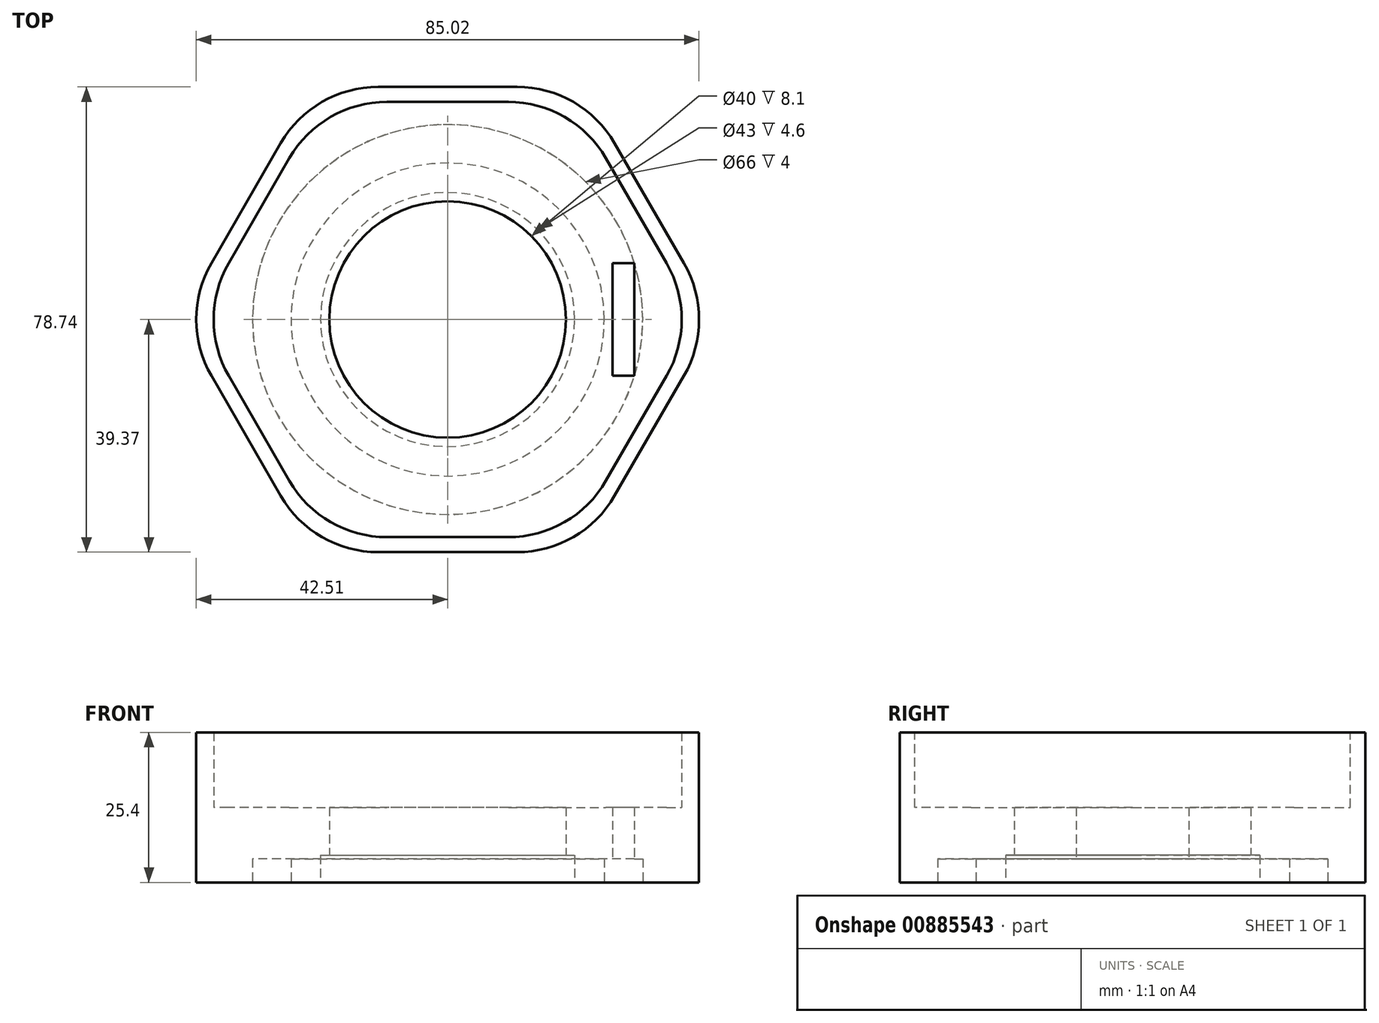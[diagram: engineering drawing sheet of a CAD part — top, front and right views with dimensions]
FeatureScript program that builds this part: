
annotation { "Feature Type Name" : "Feature", "Feature Type Description" : "" }
export const myFeature = defineFeature(function(context is Context, id is Id, definition is map)
    precondition{}
    {
        {
            var Q0;
            Q0=qCreatedBy(makeId("Top.planeOp"),FACE);
            var sketch = newSketch(context, id + "F0", { "sketchPlane" : qUnion([Q0])});
            skCircle(sketch, "E0.cCircle", {"center": v(0, 0) * mm, "radius": 39.37 * mm, "construction": true});
            skLineSegment(sketch, "E0.0", {"start": v(-22.73, 39.37) * mm, "end": v(22.73, 39.37) * mm});
            skLineSegment(sketch, "E0.1", {"start": v(22.73, 39.37) * mm, "end": v(45.46, 0) * mm});
            skLineSegment(sketch, "E0.2", {"start": v(45.46, 0) * mm, "end": v(22.73, -39.37) * mm});
            skLineSegment(sketch, "E0.3", {"start": v(22.73, -39.37) * mm, "end": v(-22.73, -39.37) * mm});
            skLineSegment(sketch, "E0.4", {"start": v(-22.73, -39.37) * mm, "end": v(-45.46, 0) * mm});
            skLineSegment(sketch, "E0.5", {"start": v(-45.46, 0) * mm, "end": v(-22.73, 39.37) * mm});
            skPoint(sketch, "E0.0.midPoint", {"position": v(0, 39.37) * mm});
            skSolve(sketch);
        }
        {
            var Q0;
            Q0=makeQuery(id+"F0.imprint","IMPRINT",FACE,{"disambiguationData":[TD([[makeQuery(id+"F0.imprint","IMPRINT",EDGE,{"derivedFrom":sQuery(id+"F0.wireOp",EDGE,"E0.0")}),-1.0]])]});
            extrude(context, id + "F1", {"entities" : qUnion([Q0]), "depth" : 25.4 * mm, "offsetDistance" : 25.4 * mm});
        }
        {
            var Q0;
            Q0=makeQuery(id+"F1.opExtrude","CAP_FACE",FACE,{"disambiguationData":[OSD([sQuery(id+"F0.wireOp",EDGE,"E0.0"),sQuery(id+"F0.wireOp",EDGE,"E0.1"),sQuery(id+"F0.wireOp",EDGE,"E0.2"),sQuery(id+"F0.wireOp",EDGE,"E0.3"),sQuery(id+"F0.wireOp",EDGE,"E0.4"),sQuery(id+"F0.wireOp",EDGE,"E0.5")])],"isStart":false});
            var sketch = newSketch(context, id + "F2", { "sketchPlane" : qUnion([Q0])});
            skCircle(sketch, "E1.cCircle", {"center": v(0, 0) * mm, "radius": 36.83 * mm, "construction": true});
            skLineSegment(sketch, "E1.0", {"start": v(-21.26, 36.83) * mm, "end": v(21.26, 36.83) * mm});
            skLineSegment(sketch, "E1.1", {"start": v(21.26, 36.83) * mm, "end": v(42.53, 0) * mm});
            skLineSegment(sketch, "E1.2", {"start": v(42.53, 0) * mm, "end": v(21.26, -36.83) * mm});
            skLineSegment(sketch, "E1.3", {"start": v(21.26, -36.83) * mm, "end": v(-21.26, -36.83) * mm});
            skLineSegment(sketch, "E1.4", {"start": v(-21.26, -36.83) * mm, "end": v(-42.53, 0) * mm});
            skLineSegment(sketch, "E1.5", {"start": v(-42.53, 0) * mm, "end": v(-21.26, 36.83) * mm});
            skPoint(sketch, "E1.0.midPoint", {"position": v(0, 36.83) * mm});
            skSolve(sketch);
        }
        {
            var Q0;
            Q0=makeQuery(id+"F2.imprint","IMPRINT",FACE,{"disambiguationData":[TD([[makeQuery(id+"F2.imprint","IMPRINT",EDGE,{"derivedFrom":sQuery(id+"F2.wireOp",EDGE,"E1.0")}),-1.0]])]});
            extrude(context, id + "F3", {"entities" : qUnion([Q0]), "operationType" : NewBodyOperationType.REMOVE, "oppositeDirection" : true, "depth" : 12.7 * mm, "offsetDistance" : 25.4 * mm});
        }
        {
            var Q0;
            Q0=makeQuery(id+"F3.boolean.opBoolean","COPY",EDGE,{"derivedFrom":makeQuery(id+"F3.opExtrude","SWEPT_EDGE",EDGE,{"disambiguationData":[OSD([sQuery(id+"F2.wireOp",EDGE,"E1.0"),sQuery(id+"F2.wireOp",EDGE,"E1.1")])]})});
            var Q1;
            Q1=makeQuery(id+"F3.boolean.opBoolean","COPY",EDGE,{"derivedFrom":makeQuery(id+"F3.opExtrude","SWEPT_EDGE",EDGE,{"disambiguationData":[OSD([sQuery(id+"F2.wireOp",EDGE,"E1.0"),sQuery(id+"F2.wireOp",EDGE,"E1.5")])]})});
            var Q2;
            Q2=makeQuery(id+"F3.boolean.opBoolean","COPY",EDGE,{"derivedFrom":makeQuery(id+"F3.opExtrude","SWEPT_EDGE",EDGE,{"disambiguationData":[OSD([sQuery(id+"F2.wireOp",EDGE,"E1.4"),sQuery(id+"F2.wireOp",EDGE,"E1.5")])]})});
            var Q3;
            Q3=makeQuery(id+"F3.boolean.opBoolean","COPY",EDGE,{"derivedFrom":makeQuery(id+"F3.opExtrude","SWEPT_EDGE",EDGE,{"disambiguationData":[OSD([sQuery(id+"F2.wireOp",EDGE,"E1.1"),sQuery(id+"F2.wireOp",EDGE,"E1.2")])]})});
            var Q4;
            Q4=makeQuery(id+"F3.boolean.opBoolean","COPY",EDGE,{"derivedFrom":makeQuery(id+"F3.opExtrude","SWEPT_EDGE",EDGE,{"disambiguationData":[OSD([sQuery(id+"F2.wireOp",EDGE,"E1.2"),sQuery(id+"F2.wireOp",EDGE,"E1.3")])]})});
            var Q5;
            Q5=makeQuery(id+"F3.boolean.opBoolean","COPY",EDGE,{"derivedFrom":makeQuery(id+"F3.opExtrude","SWEPT_EDGE",EDGE,{"disambiguationData":[OSD([sQuery(id+"F2.wireOp",EDGE,"E1.3"),sQuery(id+"F2.wireOp",EDGE,"E1.4")])]})});
            fillet(context, id + "F4", {"entities" : qUnion([Q0, Q1, Q2, Q3, Q4, Q5]), "radius" : 19.05 * mm, "tangentPropagation" : true, "allowEdgeOverflow" : false});
        }
        {
            var Q0;
            Q0=makeQuery(id+"F1.opExtrude","SWEPT_EDGE",EDGE,{"disambiguationData":[OSD([sQuery(id+"F0.wireOp",EDGE,"E0.3"),sQuery(id+"F0.wireOp",EDGE,"E0.4")])]});
            var Q1;
            Q1=makeQuery(id+"F1.opExtrude","SWEPT_EDGE",EDGE,{"disambiguationData":[OSD([sQuery(id+"F0.wireOp",EDGE,"E0.2"),sQuery(id+"F0.wireOp",EDGE,"E0.3")])]});
            var Q2;
            Q2=makeQuery(id+"F1.opExtrude","SWEPT_EDGE",EDGE,{"disambiguationData":[OSD([sQuery(id+"F0.wireOp",EDGE,"E0.1"),sQuery(id+"F0.wireOp",EDGE,"E0.2")])]});
            var Q3;
            Q3=makeQuery(id+"F1.opExtrude","SWEPT_EDGE",EDGE,{"disambiguationData":[OSD([sQuery(id+"F0.wireOp",EDGE,"E0.4"),sQuery(id+"F0.wireOp",EDGE,"E0.5")])]});
            var Q4;
            Q4=makeQuery(id+"F1.opExtrude","SWEPT_EDGE",EDGE,{"disambiguationData":[OSD([sQuery(id+"F0.wireOp",EDGE,"E0.0"),sQuery(id+"F0.wireOp",EDGE,"E0.5")])]});
            var Q5;
            Q5=makeQuery(id+"F1.opExtrude","SWEPT_EDGE",EDGE,{"disambiguationData":[OSD([sQuery(id+"F0.wireOp",EDGE,"E0.0"),sQuery(id+"F0.wireOp",EDGE,"E0.1")])]});
            fillet(context, id + "F5", {"entities" : qUnion([Q0, Q1, Q2, Q3, Q4, Q5]), "radius" : 19.05 * mm, "tangentPropagation" : true, "allowEdgeOverflow" : false});
        }
        {
            var Q0;
            Q0=makeQuery(id+"F1.opExtrude","CAP_FACE",FACE,{"disambiguationData":[OSD([sQuery(id+"F0.wireOp",EDGE,"E0.0"),sQuery(id+"F0.wireOp",EDGE,"E0.1"),sQuery(id+"F0.wireOp",EDGE,"E0.2"),sQuery(id+"F0.wireOp",EDGE,"E0.3"),sQuery(id+"F0.wireOp",EDGE,"E0.4"),sQuery(id+"F0.wireOp",EDGE,"E0.5")])],"isStart":true});
            var sketch = newSketch(context, id + "F6", { "sketchPlane" : qUnion([Q0])});
            skCircle(sketch, "E2", {"center": v(0, 0) * mm, "radius": 20 * mm});
            skSolve(sketch);
        }
        {
            var Q0;
            Q0=makeQuery(id+"F6.imprint","IMPRINT",FACE,{"disambiguationData":[TD([[makeQuery(id+"F6.imprint","IMPRINT",EDGE,{"derivedFrom":sQuery(id+"F6.wireOp",EDGE,"E2")}),1.0]])]});
            var Q1;
            Q1=makeQuery(id+"F3.boolean.opBoolean","COPY",FACE,{"derivedFrom":makeQuery(id+"F3.opExtrude","CAP_FACE",FACE,{"disambiguationData":[OSD([sQuery(id+"F2.wireOp",EDGE,"E1.0"),sQuery(id+"F2.wireOp",EDGE,"E1.1"),sQuery(id+"F2.wireOp",EDGE,"E1.2"),sQuery(id+"F2.wireOp",EDGE,"E1.3"),sQuery(id+"F2.wireOp",EDGE,"E1.4"),sQuery(id+"F2.wireOp",EDGE,"E1.5")])],"isStart":false})});
            extrude(context, id + "F7", {"entities" : qUnion([Q0]), "operationType" : NewBodyOperationType.REMOVE, "endBound" : BoundingType.UP_TO_SURFACE, "oppositeDirection" : true, "depth" : 25.4 * mm, "endBoundEntityFace" : qUnion([Q1]), "offsetDistance" : 25.4 * mm});
        }
        {
            var Q0;
            Q0=makeQuery(id+"F1.opExtrude","CAP_FACE",FACE,{"disambiguationData":[OSD([sQuery(id+"F0.wireOp",EDGE,"E0.0"),sQuery(id+"F0.wireOp",EDGE,"E0.1"),sQuery(id+"F0.wireOp",EDGE,"E0.2"),sQuery(id+"F0.wireOp",EDGE,"E0.3"),sQuery(id+"F0.wireOp",EDGE,"E0.4"),sQuery(id+"F0.wireOp",EDGE,"E0.5")])],"isStart":true});
            var sketch = newSketch(context, id + "F8", { "sketchPlane" : qUnion([Q0])});
            skCircle(sketch, "E3", {"center": v(0, 0) * mm, "radius": 21.5 * mm});
            skSolve(sketch);
        }
        {
            var Q0;
            Q0=makeQuery(id+"F8.imprint","IMPRINT",FACE,{"disambiguationData":[TD([[makeQuery(id+"F8.imprint","IMPRINT",EDGE,{"derivedFrom":sQuery(id+"F8.wireOp",EDGE,"E3")}),1.0]])]});
            extrude(context, id + "F9", {"entities" : qUnion([Q0]), "operationType" : NewBodyOperationType.REMOVE, "oppositeDirection" : true, "depth" : 4.6 * mm, "offsetDistance" : 25.4 * mm});
        }
        {
            var Q0;
            Q0=makeQuery(id+"F1.opExtrude","CAP_FACE",FACE,{"disambiguationData":[OSD([sQuery(id+"F0.wireOp",EDGE,"E0.0"),sQuery(id+"F0.wireOp",EDGE,"E0.1"),sQuery(id+"F0.wireOp",EDGE,"E0.2"),sQuery(id+"F0.wireOp",EDGE,"E0.3"),sQuery(id+"F0.wireOp",EDGE,"E0.4"),sQuery(id+"F0.wireOp",EDGE,"E0.5")])],"isStart":true});
            var sketch = newSketch(context, id + "F10", { "sketchPlane" : qUnion([Q0])});
            skCircle(sketch, "E4", {"center": v(0, 0) * mm, "radius": 33 * mm});
            skCircle(sketch, "E5", {"center": v(0, 0) * mm, "radius": 26.5 * mm});
            skSolve(sketch);
        }
        {
            var Q0;
            Q0=makeQuery(id+"F10.imprint","IMPRINT",FACE,{"disambiguationData":[TD([[makeQuery(id+"F10.imprint","IMPRINT",EDGE,{"derivedFrom":sQuery(id+"F10.wireOp",EDGE,"E4")}),1.0]])]});
            extrude(context, id + "F11", {"entities" : qUnion([Q0]), "operationType" : NewBodyOperationType.REMOVE, "oppositeDirection" : true, "depth" : 4 * mm, "offsetDistance" : 25.4 * mm});
        }
        {
            var Q0;
            Q0=makeQuery(id+"F11.boolean.opBoolean","COPY",FACE,{"derivedFrom":makeQuery(id+"F11.opExtrude","CAP_FACE",FACE,{"disambiguationData":[OSD([sQuery(id+"F10.wireOp",EDGE,"E4"),sQuery(id+"F10.wireOp",EDGE,"E5")])],"isStart":false})});
            var sketch = newSketch(context, id + "F12", { "sketchPlane" : qUnion([Q0])});
            skLineSegment(sketch, "E6", {"start": v(26.5, 0) * mm, "end": v(33, 0) * mm});
            skLineSegment(sketch, "E7.bottom", {"start": v(31.6, 9.53) * mm, "end": v(27.9, 9.53) * mm});
            skLineSegment(sketch, "E7.top", {"start": v(31.6, -9.53) * mm, "end": v(27.9, -9.53) * mm});
            skLineSegment(sketch, "E7.left", {"start": v(31.6, 9.53) * mm, "end": v(31.6, -9.53) * mm});
            skLineSegment(sketch, "E7.right", {"start": v(27.9, 9.53) * mm, "end": v(27.9, -9.53) * mm});
            skPoint(sketch, "E7.middle", {"position": v(29.75, 0) * mm});
            skSolve(sketch);
        }
        {
            var Q0;
            {var subQ5=sQuery(id+"F12.wireOp",EDGE,"E7.bottom");Q0=makeQuery(id+"F12.imprint","IMPRINT",FACE,{"disambiguationData":[TD([[makeQuery(id+"F12.imprint","IMPRINT",EDGE,{"derivedFrom":subQ5}),1.0]])]});}
            var Q1;
            {var subQ5=sQuery(id+"F12.wireOp",EDGE,"E7.top");Q1=makeQuery(id+"F12.imprint","IMPRINT",FACE,{"disambiguationData":[TD([[makeQuery(id+"F12.imprint","IMPRINT",EDGE,{"derivedFrom":subQ5}),-1.0]])]});}
            var Q2;
            Q2=makeQuery(id+"F3.boolean.opBoolean","COPY",FACE,{"derivedFrom":makeQuery(id+"F3.opExtrude","CAP_FACE",FACE,{"disambiguationData":[OSD([sQuery(id+"F2.wireOp",EDGE,"E1.0"),sQuery(id+"F2.wireOp",EDGE,"E1.1"),sQuery(id+"F2.wireOp",EDGE,"E1.2"),sQuery(id+"F2.wireOp",EDGE,"E1.3"),sQuery(id+"F2.wireOp",EDGE,"E1.4"),sQuery(id+"F2.wireOp",EDGE,"E1.5")])],"isStart":false})});
            extrude(context, id + "F13", {"entities" : qUnion([Q0, Q1]), "operationType" : NewBodyOperationType.REMOVE, "endBound" : BoundingType.UP_TO_SURFACE, "oppositeDirection" : true, "depth" : 25.4 * mm, "endBoundEntityFace" : qUnion([Q2]), "offsetDistance" : 25.4 * mm});
        }
    });
